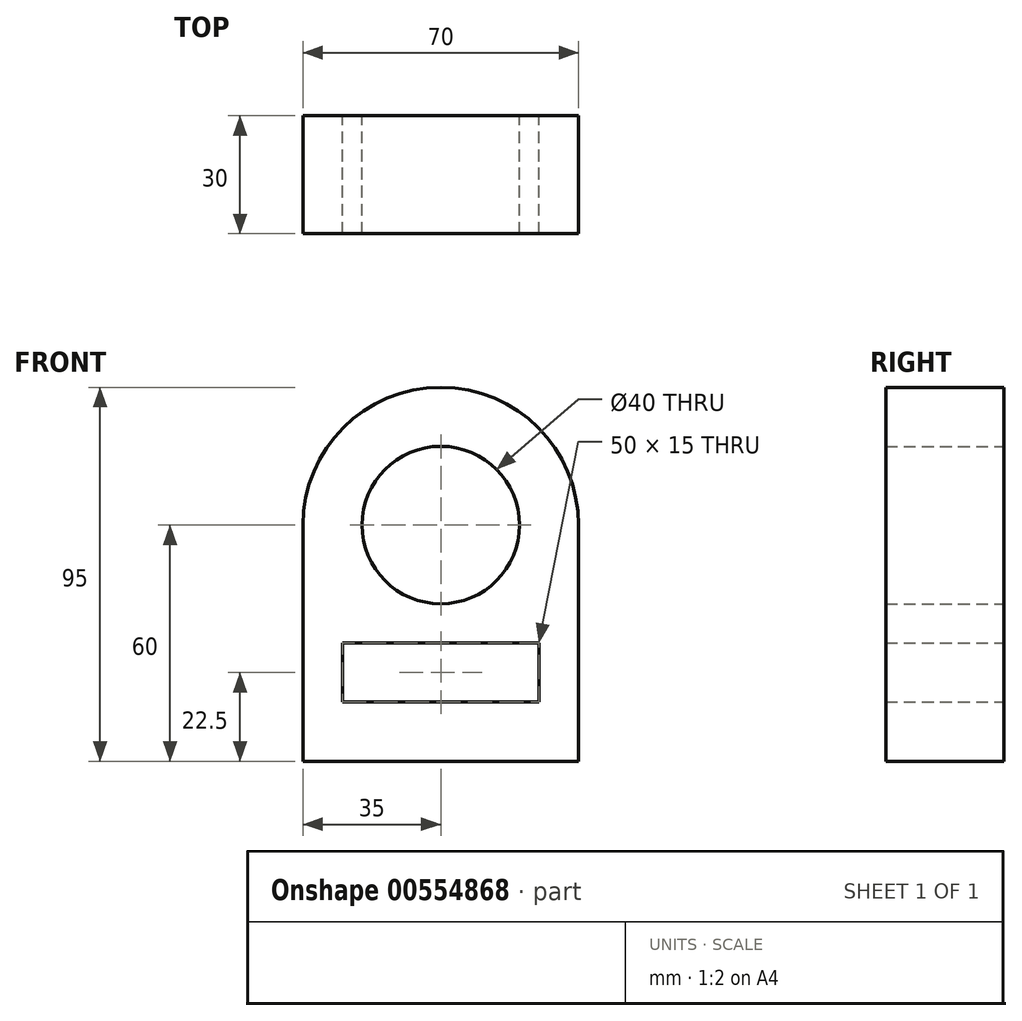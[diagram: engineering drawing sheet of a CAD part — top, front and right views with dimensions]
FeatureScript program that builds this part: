
annotation { "Feature Type Name" : "Feature", "Feature Type Description" : "" }
export const myFeature = defineFeature(function(context is Context, id is Id, definition is map)
    precondition{}
    {
        {
            var Q0;
            Q0=qCreatedBy(makeId("Front.planeOp"),FACE);
            var sketch = newSketch(context, id + "F0", { "sketchPlane" : qUnion([Q0])});
            skCircle(sketch, "E0", {"center": v(0, 0) * mm, "radius": 20 * mm});
            skArc(sketch, "E1", {"start": v(35, 0) * mm, "mid": v(0, 35) * mm, "end": v(-35, 0) * mm});
            skLineSegment(sketch, "E2", {"start": v(-35, 0) * mm, "end": v(-35, -60) * mm});
            skLineSegment(sketch, "E3", {"start": v(35, 0) * mm, "end": v(35, -60) * mm});
            skLineSegment(sketch, "E4", {"start": v(35, -60) * mm, "end": v(-35, -60) * mm});
            skPoint(sketch, "E5.firstSnap0", {"position": v(-35, -30) * mm});
            skLineSegment(sketch, "E5.bottom", {"start": v(-25, -30) * mm, "end": v(25, -30) * mm});
            skLineSegment(sketch, "E5.top", {"start": v(-25, -45) * mm, "end": v(25, -45) * mm});
            skLineSegment(sketch, "E5.left", {"start": v(-25, -30) * mm, "end": v(-25, -45) * mm});
            skLineSegment(sketch, "E5.right", {"start": v(25, -30) * mm, "end": v(25, -45) * mm});
            skSolve(sketch);
        }
        {
            var Q0;
            Q0 = qSketchRegion(id + "F0", true);
            var Q1;
            Q1=makeQuery(id+"F0.imprint","IMPRINT",FACE,{"disambiguationData":[TD([[makeQuery(id+"F0.imprint","IMPRINT",EDGE,{"derivedFrom":sQuery(id+"F0.wireOp",EDGE,"E0")}),-1.0]])]});
            extrude(context, id + "F1", {"entities" : qUnion([Q0, Q1]), "depth" : 30 * mm, "offsetDistance" : 25 * mm});
        }
    });
